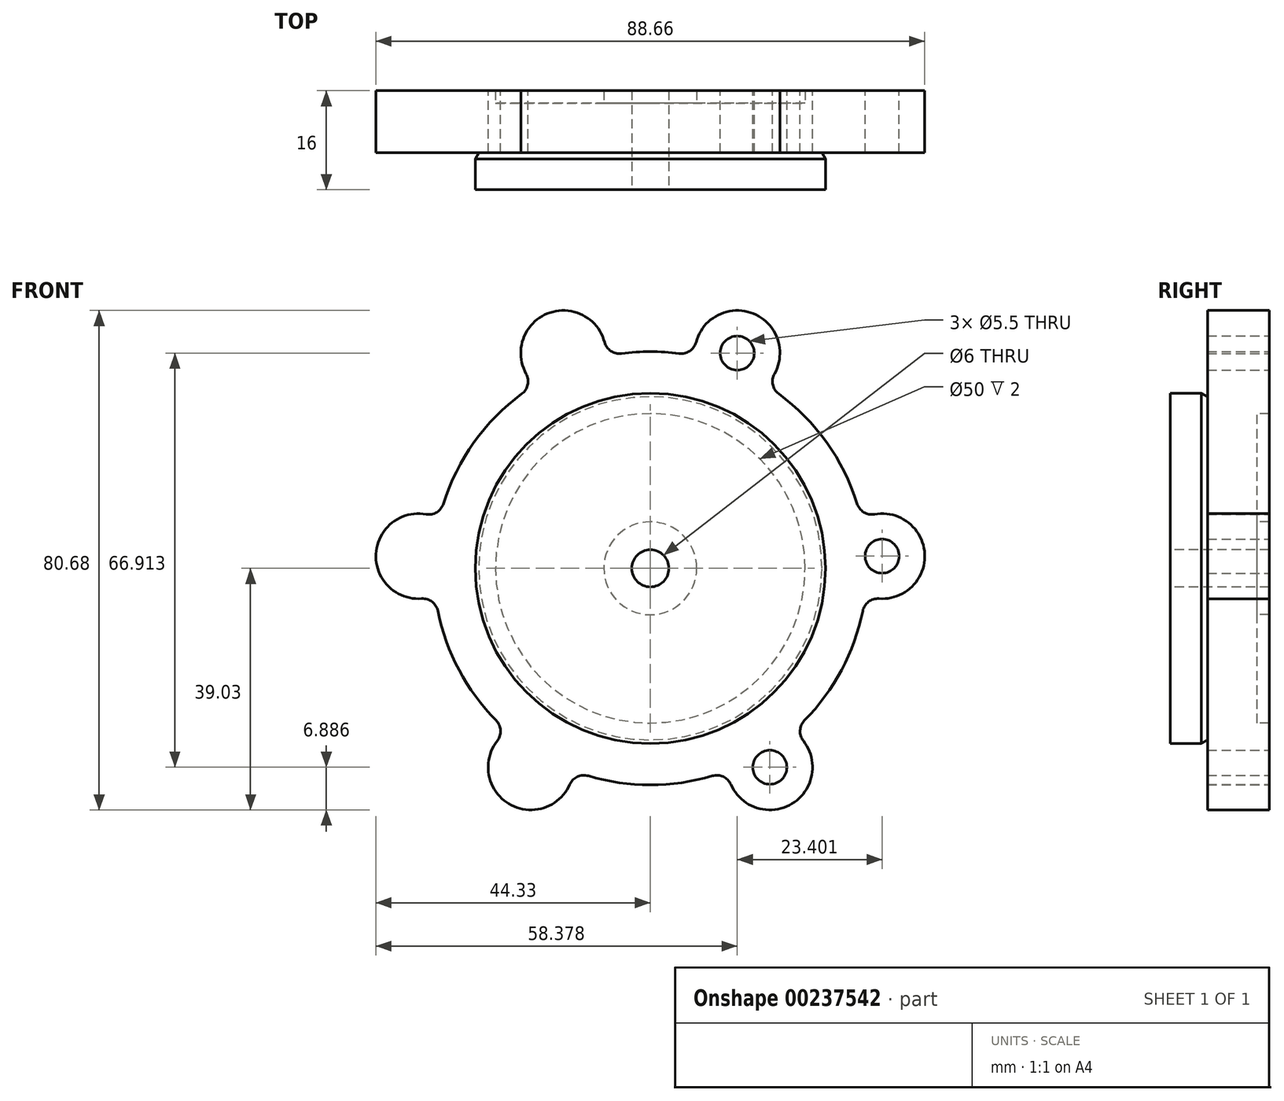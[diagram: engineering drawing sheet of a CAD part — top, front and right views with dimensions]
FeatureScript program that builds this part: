
annotation { "Feature Type Name" : "Feature", "Feature Type Description" : "" }
export const myFeature = defineFeature(function(context is Context, id is Id, definition is map)
    precondition{}
    {
        {
            var Q0;
            Q0=qCreatedBy(makeId("Right.planeOp"),FACE);
            var sketch = newSketch(context, id + "F0", { "sketchPlane" : qUnion([Q0])});
            skLineSegment(sketch, "E0", {"start": v(0, -15.89) * mm, "end": v(0, 23.93) * mm, "construction": true});
            skLineSegment(sketch, "E1", {"start": v(8.84, 3) * mm, "end": v(-7.16, 3) * mm});
            skLineSegment(sketch, "E2", {"start": v(-7.16, 3) * mm, "end": v(-7.16, 28.3) * mm});
            skLineSegment(sketch, "E3", {"start": v(-7.16, 28.3) * mm, "end": v(-2.16, 28.3) * mm});
            skLineSegment(sketch, "E4", {"start": v(-2.16, 28.3) * mm, "end": v(-1.16, 27.72) * mm});
            skLineSegment(sketch, "E5", {"start": v(-1.16, 27.72) * mm, "end": v(-1.16, 44.38) * mm});
            skLineSegment(sketch, "E6", {"start": v(-1.16, 44.38) * mm, "end": v(8.84, 44.38) * mm});
            skLineSegment(sketch, "E7", {"start": v(8.84, 44.38) * mm, "end": v(8.84, 25) * mm});
            skLineSegment(sketch, "E8", {"start": v(8.84, 25) * mm, "end": v(6.84, 25) * mm});
            skLineSegment(sketch, "E9", {"start": v(6.84, 25) * mm, "end": v(6.84, 7.5) * mm});
            skLineSegment(sketch, "E10", {"start": v(6.84, 7.5) * mm, "end": v(8.84, 7.5) * mm});
            skLineSegment(sketch, "E11", {"start": v(8.84, 7.5) * mm, "end": v(8.84, 3) * mm});
            skLineSegment(sketch, "E12", {"start": v(0, 0) * mm, "end": v(29.33, 0) * mm, "construction": true});
            skSolve(sketch);
        }
        {
            var Q0;
            Q0=makeQuery(id+"F0.imprint","IMPRINT",FACE,{"disambiguationData":[TD([[makeQuery(id+"F0.imprint","IMPRINT",EDGE,{"derivedFrom":sQuery(id+"F0.wireOp",EDGE,"E1")}),-1.0]])]});
            var Q1;
            Q1=sQuery(id+"F0.wireOp",EDGE,"E12");
            revolve(context, id + "F1", {"entities" : qUnion([Q0]), "axis" : qUnion([Q1]), "revolveType" : RevolveType.FULL});
        }
        {
            var Q0;
            Q0=makeQuery(id+"F1.opRevolve","SWEPT_FACE",FACE,{"disambiguationData":[OSD([sQuery(id+"F0.wireOp",EDGE,"E7")])]});
            var sketch = newSketch(context, id + "F2", { "sketchPlane" : qUnion([Q0])});
            skLineSegment(sketch, "E13", {"start": v(0, 0) * mm, "end": v(0, 35.38) * mm, "construction": true});
            skLineSegment(sketch, "E14", {"start": v(0, 0) * mm, "end": v(-14.05, 34.77) * mm, "construction": true});
            skCircle(sketch, "E15", {"center": v(0, 0) * mm, "radius": 37.5 * mm, "construction": true});
            skArc(sketch, "E16", {"start": v(-20.76, 28.18) * mm, "mid": v(-28.5, 20.32) * mm, "end": v(-33.4, 10.45) * mm});
            skCircle(sketch, "E17", {"center": v(-14.05, 34.77) * mm, "radius": 2.75 * mm});
            skArc(sketch, "E18", {"start": v(-7.4, 36.53) * mm, "mid": v(-16.63, 41.15) * mm, "end": v(-20.06, 31.41) * mm});
            skLineSegment(sketch, "E19", {"start": v(0, 0) * mm, "end": v(-37.45, 1.96) * mm, "construction": true});
            skLineSegment(sketch, "E20", {"start": v(0, 0) * mm, "end": v(-19.31, -32.14) * mm, "construction": true});
            skArc(sketch, "E21", {"start": v(-36.23, 8.74) * mm, "mid": v(-44.32, 2.32) * mm, "end": v(-36.95, -4.9) * mm});
            skArc(sketch, "E22", {"start": v(-24.72, -27.89) * mm, "mid": v(-22.86, -38.04) * mm, "end": v(-13.02, -34.92) * mm});
            skCircle(sketch, "E23", {"center": v(-19.31, -32.14) * mm, "radius": 2.75 * mm});
            skCircle(sketch, "E24", {"center": v(-37.45, 1.96) * mm, "radius": 2.75 * mm});
            skCircle(sketch, "E25.MirrorC", {"center": v(19.31, -32.14) * mm, "radius": 2.75 * mm});
            skArc(sketch, "E26.MirrorC", {"start": v(24.72, -27.89) * mm, "mid": v(22.86, -38.04) * mm, "end": v(13.02, -34.92) * mm});
            skCircle(sketch, "E27.MirrorC", {"center": v(37.45, 1.96) * mm, "radius": 2.75 * mm});
            skArc(sketch, "E28.MirrorC", {"start": v(36.23, 8.74) * mm, "mid": v(44.32, 2.32) * mm, "end": v(36.95, -4.9) * mm});
            skCircle(sketch, "E29.MirrorC", {"center": v(14.05, 34.77) * mm, "radius": 2.75 * mm});
            skArc(sketch, "E30.MirrorC", {"start": v(7.4, 36.53) * mm, "mid": v(16.63, 41.15) * mm, "end": v(20.06, 31.41) * mm});
            skArc(sketch, "E31.trimOffspring", {"start": v(4.64, 34.7) * mm, "mid": v(0, 35) * mm, "end": v(-4.64, 34.7) * mm});
            skArc(sketch, "E32.trimOffspring", {"start": v(33.4, 10.45) * mm, "mid": v(28.5, 20.32) * mm, "end": v(20.76, 28.18) * mm});
            skArc(sketch, "E33.trimOffspring", {"start": v(24.91, -24.59) * mm, "mid": v(30.9, -16.43) * mm, "end": v(34.31, -6.9) * mm});
            skArc(sketch, "E34.trimOffspring", {"start": v(-10.01, -33.54) * mm, "mid": v(0, -35) * mm, "end": v(10.01, -33.54) * mm});
            skArc(sketch, "E35.trimOffspring", {"start": v(-34.31, -6.9) * mm, "mid": v(-30.9, -16.43) * mm, "end": v(-24.91, -24.59) * mm});
            skPoint(sketch, "E36.visualSharp", {"position": v(-18.63, 29.63) * mm});
            skArc(sketch, "E36.filletArc", {"start": v(-20.76, 28.18) * mm, "mid": v(-19.8, 29.66) * mm, "end": v(-20.06, 31.41) * mm});
            skPoint(sketch, "E37.visualSharp", {"position": v(-7.18, 34.26) * mm});
            skArc(sketch, "E37.filletArc", {"start": v(-7.4, 36.53) * mm, "mid": v(-6.37, 35.1) * mm, "end": v(-4.64, 34.7) * mm});
            skPoint(sketch, "E38.visualSharp", {"position": v(7.18, 34.26) * mm});
            skArc(sketch, "E38.filletArc", {"start": v(4.64, 34.7) * mm, "mid": v(6.37, 35.1) * mm, "end": v(7.4, 36.53) * mm});
            skPoint(sketch, "E39.visualSharp", {"position": v(18.63, 29.63) * mm});
            skArc(sketch, "E39.filletArc", {"start": v(20.06, 31.41) * mm, "mid": v(19.8, 29.66) * mm, "end": v(20.76, 28.18) * mm});
            skPoint(sketch, "E40.visualSharp", {"position": v(34.08, 7.97) * mm});
            skArc(sketch, "E40.filletArc", {"start": v(33.4, 10.45) * mm, "mid": v(34.5, 9.06) * mm, "end": v(36.23, 8.74) * mm});
            skPoint(sketch, "E41.visualSharp", {"position": v(-34.08, 7.97) * mm});
            skArc(sketch, "E41.filletArc", {"start": v(-36.23, 8.74) * mm, "mid": v(-34.5, 9.06) * mm, "end": v(-33.4, 10.45) * mm});
            skPoint(sketch, "E42.visualSharp", {"position": v(34.73, -4.36) * mm});
            skArc(sketch, "E42.filletArc", {"start": v(36.95, -4.9) * mm, "mid": v(35.25, -5.4) * mm, "end": v(34.31, -6.9) * mm});
            skPoint(sketch, "E43.visualSharp", {"position": v(-34.73, -4.36) * mm});
            skArc(sketch, "E43.filletArc", {"start": v(-34.31, -6.9) * mm, "mid": v(-35.25, -5.4) * mm, "end": v(-36.95, -4.9) * mm});
            skPoint(sketch, "E44.visualSharp", {"position": v(23.03, -26.35) * mm});
            skArc(sketch, "E44.filletArc", {"start": v(24.91, -24.59) * mm, "mid": v(24.2, -26.2) * mm, "end": v(24.72, -27.89) * mm});
            skPoint(sketch, "E45.visualSharp", {"position": v(12.45, -32.7) * mm});
            skArc(sketch, "E45.filletArc", {"start": v(13.02, -34.92) * mm, "mid": v(11.78, -33.66) * mm, "end": v(10.01, -33.54) * mm});
            skPoint(sketch, "E46.visualSharp", {"position": v(-12.45, -32.7) * mm});
            skArc(sketch, "E46.filletArc", {"start": v(-10.01, -33.54) * mm, "mid": v(-11.78, -33.66) * mm, "end": v(-13.02, -34.92) * mm});
            skPoint(sketch, "E47.visualSharp", {"position": v(-23.03, -26.35) * mm});
            skArc(sketch, "E47.filletArc", {"start": v(-24.72, -27.89) * mm, "mid": v(-24.2, -26.2) * mm, "end": v(-24.91, -24.59) * mm});
            skSolve(sketch);
        }
        {
            var Q0;
            Q0=makeQuery(id+"F2.imprint","IMPRINT",FACE,{"disambiguationData":[TD([[makeQuery(id+"F2.imprint","IMPRINT",EDGE,{"derivedFrom":sQuery(id+"F2.wireOp",EDGE,"E16")}),-1.0]])]});
            var Q1;
            Q1=makeQuery(id+"F2.imprint","IMPRINT",FACE,{"disambiguationData":[TD([[makeQuery(id+"F2.imprint","IMPRINT",EDGE,{"derivedFrom":sQuery(id+"F2.wireOp",EDGE,"E35.trimOffspring")}),-1.0]])]});
            var Q2;
            Q2=makeQuery(id+"F2.imprint","IMPRINT",FACE,{"disambiguationData":[TD([[makeQuery(id+"F2.imprint","IMPRINT",EDGE,{"derivedFrom":sQuery(id+"F2.wireOp",EDGE,"E34.trimOffspring")}),-1.0]])]});
            var Q3;
            Q3=makeQuery(id+"F2.imprint","IMPRINT",FACE,{"disambiguationData":[TD([[makeQuery(id+"F2.imprint","IMPRINT",EDGE,{"derivedFrom":sQuery(id+"F2.wireOp",EDGE,"E33.trimOffspring")}),-1.0]])]});
            var Q4;
            Q4=makeQuery(id+"F2.imprint","IMPRINT",FACE,{"disambiguationData":[TD([[makeQuery(id+"F2.imprint","IMPRINT",EDGE,{"derivedFrom":sQuery(id+"F2.wireOp",EDGE,"E32.trimOffspring")}),-1.0]])]});
            var Q5;
            Q5=makeQuery(id+"F2.imprint","IMPRINT",FACE,{"disambiguationData":[TD([[makeQuery(id+"F2.imprint","IMPRINT",EDGE,{"derivedFrom":sQuery(id+"F2.wireOp",EDGE,"E31.trimOffspring")}),-1.0]])]});
            var Q6;
            Q6=makeQuery(id+"F2.imprint","IMPRINT",FACE,{"disambiguationData":[TD([[makeQuery(id+"F2.imprint","IMPRINT",EDGE,{"derivedFrom":sQuery(id+"F2.wireOp",EDGE,"E17")}),1.0]])]});
            var Q7;
            Q7=makeQuery(id+"F2.imprint","IMPRINT",FACE,{"disambiguationData":[TD([[makeQuery(id+"F2.imprint","IMPRINT",EDGE,{"derivedFrom":sQuery(id+"F2.wireOp",EDGE,"E29.MirrorC")}),-1.0]])]});
            var Q8;
            Q8=makeQuery(id+"F2.imprint","IMPRINT",FACE,{"disambiguationData":[TD([[makeQuery(id+"F2.imprint","IMPRINT",EDGE,{"derivedFrom":sQuery(id+"F2.wireOp",EDGE,"E27.MirrorC")}),-1.0]])]});
            var Q9;
            Q9=makeQuery(id+"F2.imprint","IMPRINT",FACE,{"disambiguationData":[TD([[makeQuery(id+"F2.imprint","IMPRINT",EDGE,{"derivedFrom":sQuery(id+"F2.wireOp",EDGE,"E25.MirrorC")}),-1.0]])]});
            var Q10;
            Q10=makeQuery(id+"F2.imprint","IMPRINT",FACE,{"disambiguationData":[TD([[makeQuery(id+"F2.imprint","IMPRINT",EDGE,{"derivedFrom":sQuery(id+"F2.wireOp",EDGE,"E23")}),1.0]])]});
            var Q11;
            Q11=makeQuery(id+"F2.imprint","IMPRINT",FACE,{"disambiguationData":[TD([[makeQuery(id+"F2.imprint","IMPRINT",EDGE,{"derivedFrom":sQuery(id+"F2.wireOp",EDGE,"E24")}),1.0]])]});
            extrude(context, id + "F3", {"entities" : qUnion([Q0, Q1, Q2, Q3, Q4, Q5, Q6, Q7, Q8, Q9, Q10, Q11]), "operationType" : NewBodyOperationType.REMOVE, "endBound" : BoundingType.UP_TO_NEXT, "oppositeDirection" : true, "depth" : 25 * mm});
        }
    });
